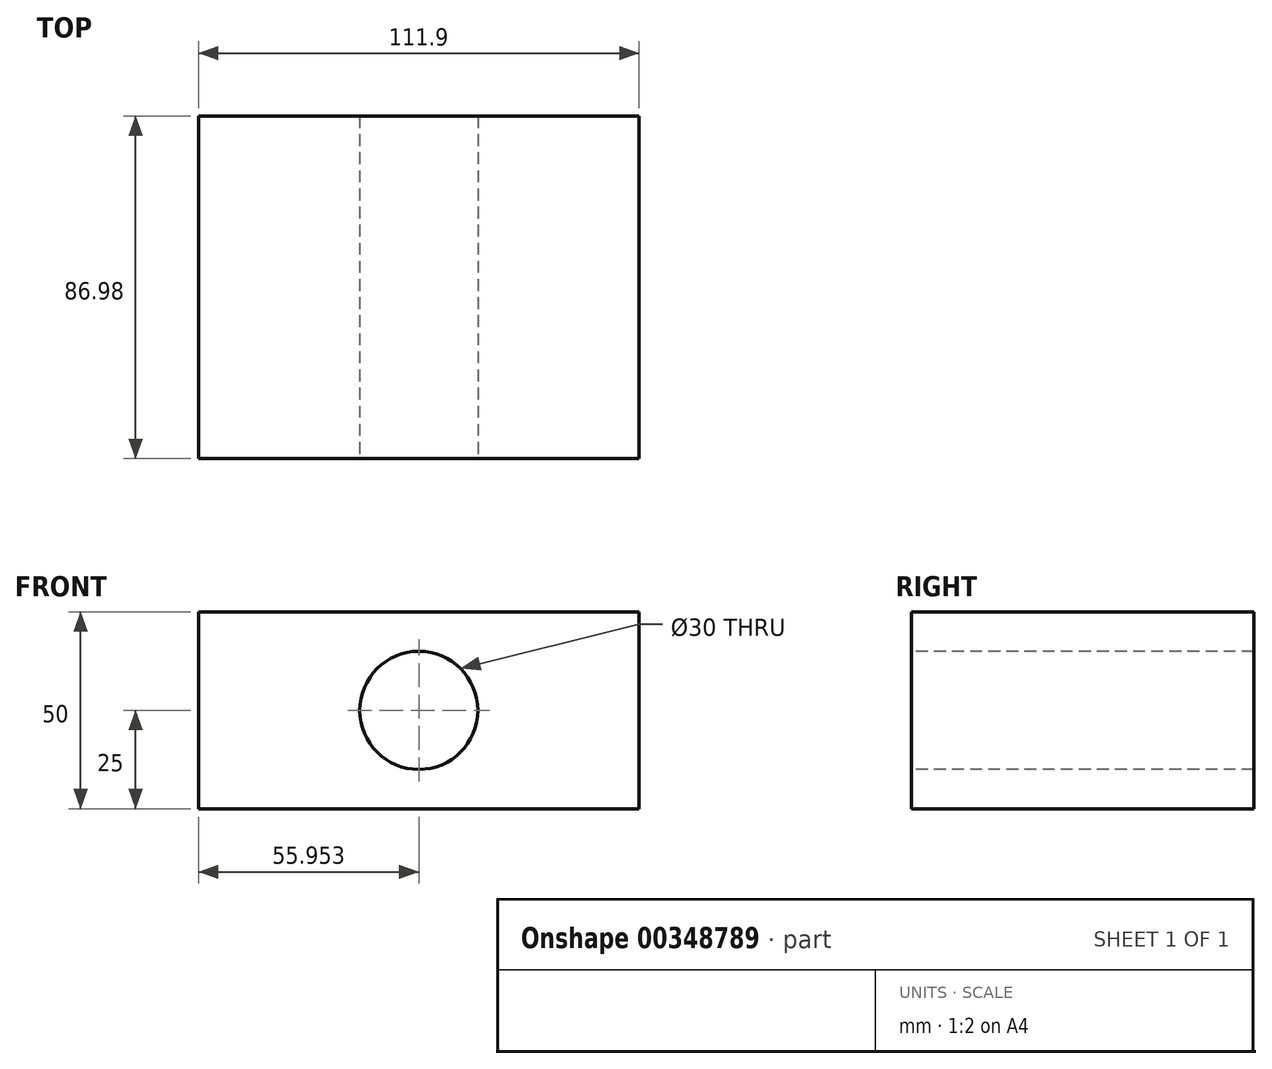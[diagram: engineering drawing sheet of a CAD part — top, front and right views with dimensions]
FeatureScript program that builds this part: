
annotation { "Feature Type Name" : "Feature", "Feature Type Description" : "" }
export const myFeature = defineFeature(function(context is Context, id is Id, definition is map)
    precondition{}
    {
        {
            var Q0;
            Q0=qCreatedBy(makeId("Top.planeOp"),FACE);
            var sketch = newSketch(context, id + "F0", { "sketchPlane" : qUnion([Q0])});
            skLineSegment(sketch, "E0.bottom", {"start": v(-49.39, 40.26) * mm, "end": v(62.51, 40.26) * mm});
            skLineSegment(sketch, "E0.top", {"start": v(-49.39, -46.72) * mm, "end": v(62.51, -46.72) * mm});
            skLineSegment(sketch, "E0.left", {"start": v(-49.39, 40.26) * mm, "end": v(-49.39, -46.72) * mm});
            skLineSegment(sketch, "E0.right", {"start": v(62.51, 40.26) * mm, "end": v(62.51, -46.72) * mm});
            skSolve(sketch);
        }
        {
            var Q0;
            Q0=makeQuery(id+"F0.imprint","IMPRINT",FACE,{"disambiguationData":[TD([[makeQuery(id+"F0.imprint","IMPRINT",EDGE,{"derivedFrom":sQuery(id+"F0.wireOp",EDGE,"E0.bottom")}),-1.0]])]});
            extrude(context, id + "F1", {"entities" : qUnion([Q0]), "depth" : 50 * mm});
        }
        {
            var Q0;
            Q0=makeQuery(id+"F1.opExtrude","SWEPT_FACE",FACE,{"disambiguationData":[OSD([sQuery(id+"F0.wireOp",EDGE,"E0.top")])]});
            var sketch = newSketch(context, id + "F2", { "sketchPlane" : qUnion([Q0])});
            skCircle(sketch, "E1", {"center": v(6.56, 25) * mm, "radius": 15 * mm});
            skLineSegment(sketch, "E2", {"start": v(-71.73, 25) * mm, "end": v(102.43, 25) * mm, "construction": true});
            skLineSegment(sketch, "E3", {"start": v(6.56, 60.92) * mm, "end": v(6.56, -39.78) * mm, "construction": true});
            skSolve(sketch);
        }
        {
            var Q0;
            Q0 = qSketchRegion(id + "F2", true);
            extrude(context, id + "F3", {"entities" : qUnion([Q0]), "operationType" : NewBodyOperationType.REMOVE, "endBound" : BoundingType.UP_TO_NEXT, "oppositeDirection" : true, "depth" : 25 * mm});
        }
    });
